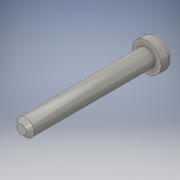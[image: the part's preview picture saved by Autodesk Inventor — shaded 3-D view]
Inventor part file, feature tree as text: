
AUTODESK INVENTOR PART (.ipt)
format: ipt  version: 2016 (Build 200138000, 138)  size: 162,304 bytes
history: native  units: mm
features: extrude x3, sketch x3, fillet x1, chamfer x1
ambient origin geometry x8: Origin, YZ Plane, XZ Plane, XY Plane, X Axis, Y Axis, Z Axis, Center Point
bodies: Solid1 (feature_tree)
feature tree (8):
  extrude  "Extrusion1"  Depth=16.0mm TaperAngle=0.0deg
  extrude  "Extrusion2"  Depth=1.5mm TaperAngle=0.0deg
  fillet  "Fillet1"  Radius=0.5mm
  extrude  "Extrusion3"  Depth=1.8mm
  chamfer  "Chamfer1"  Distance=1.8mm
  sketch  "Sketch1"  dims[d0=2.2mm d1=16.0mm d2=0.0mm]
  sketch  "Sketch2"  dims[d3=3.7mm d4=1.5mm d5=0.0mm d6=0.5mm]
  sketch  "Sketch3"  dims[d7=0.6mm d8=1.8mm d9=1.8mm d10=0.6mm d11=0.6mm d12=0.6mm d13=0.6mm d14=0.6mm d15=1.5mm d16=0.0mm d17=0.5mm d18=2.0mm d19=45.0deg]
